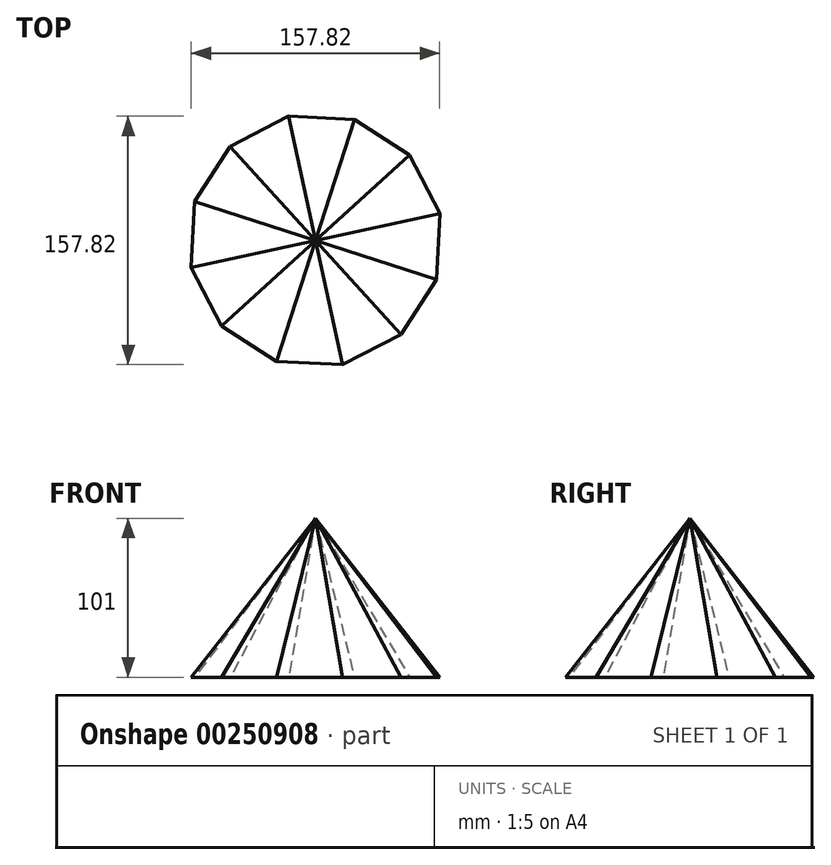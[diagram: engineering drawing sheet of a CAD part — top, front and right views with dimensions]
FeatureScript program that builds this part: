
annotation { "Feature Type Name" : "Feature", "Feature Type Description" : "" }
export const myFeature = defineFeature(function(context is Context, id is Id, definition is map)
    precondition{}
    {
        {
            var Q0;
            Q0=qCreatedBy(makeId("Top.planeOp"),FACE);
            var sketch = newSketch(context, id + "F0", { "sketchPlane" : qUnion([Q0])});
            skCircle(sketch, "E0.cCircle", {"center": v(0, 0) * mm, "radius": 80.73 * mm, "construction": true});
            skLineSegment(sketch, "E0.0", {"start": v(54.22, -59.82) * mm, "end": v(17.05, -78.91) * mm});
            skLineSegment(sketch, "E0.1", {"start": v(17.05, -78.91) * mm, "end": v(-24.7, -76.86) * mm});
            skLineSegment(sketch, "E0.2", {"start": v(-24.7, -76.86) * mm, "end": v(-59.82, -54.22) * mm});
            skLineSegment(sketch, "E0.3", {"start": v(-59.82, -54.22) * mm, "end": v(-78.91, -17.05) * mm});
            skLineSegment(sketch, "E0.4", {"start": v(-78.91, -17.05) * mm, "end": v(-76.86, 24.7) * mm});
            skLineSegment(sketch, "E0.5", {"start": v(-76.86, 24.7) * mm, "end": v(-54.22, 59.82) * mm});
            skLineSegment(sketch, "E0.6", {"start": v(-54.22, 59.82) * mm, "end": v(-17.05, 78.91) * mm});
            skLineSegment(sketch, "E0.7", {"start": v(-17.05, 78.91) * mm, "end": v(24.7, 76.86) * mm});
            skLineSegment(sketch, "E0.8", {"start": v(24.7, 76.86) * mm, "end": v(59.82, 54.22) * mm});
            skLineSegment(sketch, "E0.9", {"start": v(59.82, 54.22) * mm, "end": v(78.91, 17.05) * mm});
            skLineSegment(sketch, "E0.10", {"start": v(78.91, 17.05) * mm, "end": v(76.86, -24.7) * mm});
            skLineSegment(sketch, "E0.11", {"start": v(76.86, -24.7) * mm, "end": v(54.22, -59.82) * mm});
            skSolve(sketch);
        }
        {
            var Q0;
            Q0=qCreatedBy(makeId("Top.planeOp"),FACE);
            cPlane(context, id + "F1", {"entities" : qUnion([Q0]), "cplaneType" : CPlaneType.OFFSET, "offset" : 101 * mm, "width" : 150 * mm, "height" : 150 * mm});
        }
        {
            var Q0;
            Q0=qCreatedBy(id+"F1.planeOp",FACE);
            var sketch = newSketch(context, id + "F2", { "sketchPlane" : qUnion([Q0])});
            skPoint(sketch, "E1", {"position": v(0, 0) * mm});
            skSolve(sketch);
        }
        {
            var Q0;
            Q0=sQuery(id+"F2.wireOp",VERTEX,"E1");
            var Q1;
            Q1=makeQuery(id+"F0.imprint","IMPRINT",FACE,{"disambiguationData":[TD([[makeQuery(id+"F0.imprint","IMPRINT",EDGE,{"derivedFrom":sQuery(id+"F0.wireOp",EDGE,"E0.0")}),-1.0]])]});
            loft(context, id + "F3", {"sheetProfilesArray" : [{ "sheetProfileEntities" : qUnion([Q0]) }, { "sheetProfileEntities" : qUnion([Q1]) }]});
        }
    });
